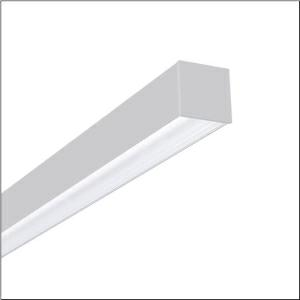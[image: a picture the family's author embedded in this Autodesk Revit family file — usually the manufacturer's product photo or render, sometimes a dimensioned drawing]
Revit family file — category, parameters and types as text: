
# Revit family: silica_r_5mx21dd1w4a_969a
name_source: partatom
category: Lighting Fixtures
units: mm (PartAtom-declared; Revit-internal decimal feet)

## family parameters
Cut with Voids When Loaded = No
Host = Face
Light Source = No
Part Type = Normal
Room Calculation Point = No
Round Connector Dimension = Use Diameter
Shared = No

## types (1)
- --- (1 x LED, 3140 lm, 22.6 W, 4000K)
    Apparent Load = 23 VA
    CIE Flux Codes = 47 79 96 100 100
    Color Rendering = 80
    Color Temperature = 4000K
    Default Elevation = 1800 mm
    Description = Silica®, office luminaire, of aluminium, opal, light emission: direct distribution, primary light characteristic: symmetric, installation type: surface-mounted, LED, rated luminous flux: 3.010lm, luminous efficacy: 123lm/W, light colour: 840, colour temperature: 4000K, control gear: ECG DALI, with terminal, 3+2-pole, max. 2.5mm², mains connection: 230V, AC, 50/60Hz, rated input power: 24W, luminaire housing, of aluminium, traffic white (RAL 9016), length: 1.442mm, width: 65mm, height: 64mm, protection rating (complete): IP20, insulation class (complete): insulation class I (protective earthing), certification: CE, permissible operating ambient temperature: 0..+35°C, standard: EN 50419, packaging unit: 1 piece
    Height = 64 mm
    Lamp = 1 x LED
    Lamp Light Flux = 3140 lm
    Lamp Power = 22.6 W
    Lamp count = 1
    Length = 1442 mm
    Luminous efficacy = 139 lm/W
    Manufacturer = Siteco
    ModVariant = No
    Model = 5MX21DD1W4A
    Mounting Place = Ceiling
    Mounting Type = Surface mounted
    Number of Poles = 1
    OnlyDefault = Yes
    Power Factor = 1
    Product Name = Silica®
    Product group = office luminaire | ceiling mounted
    ProductGroupID = 300
    Protection Class = Protection class I
    Protection Degree = IP 20
    RLX_Detail_Level = 1
    RLX_Emergency_Light_Flux = 0 lm
    RLX_Emergency_Type = 0
    RLX_Emergency_Type_DB = No
    RlxData = <blob elided: 22721 chars, md5=8cbb2356>
    Socket = socket
    Standby Power = 0 W
    System Light Flux = 3140 lm
    System Power = 23 W
    Type Comments = factory setting: luminous flux: 100 % | dim-lin: 254 | 125 mA
    Type Image = l_248206.jpg
    URL = http://relux.com
    VarID = @adj_152873
    Voltage = 0 V
    Weight = 0.00 kg
    Width = 65 mm

## geometry (parser evidence)
native form markers: Blend x4, Sweep x9
no freeform markers — native parametric forms only
